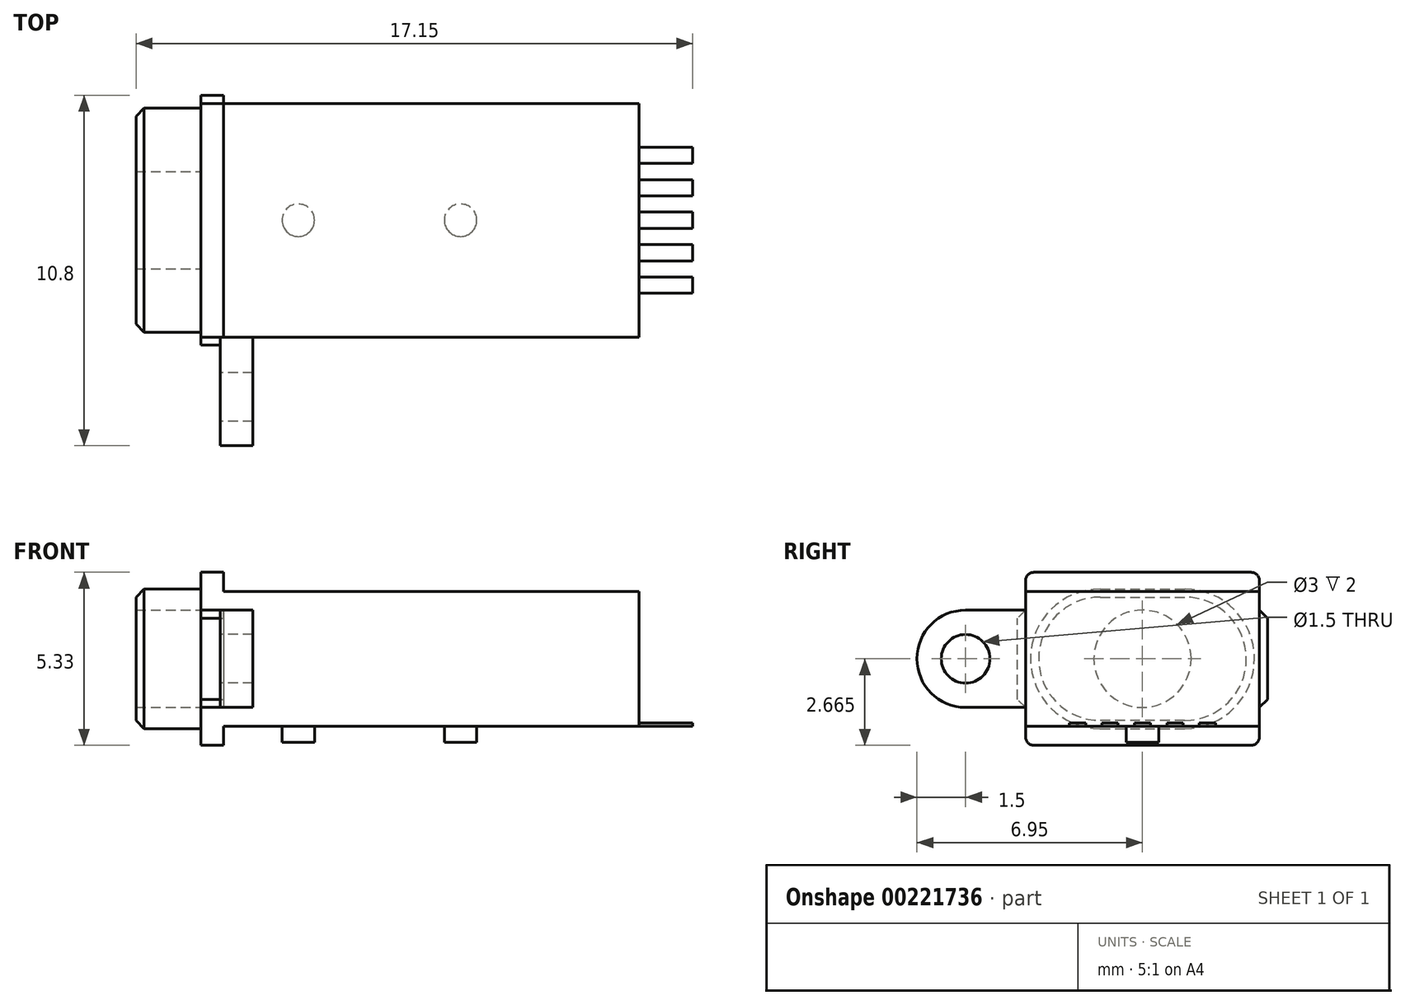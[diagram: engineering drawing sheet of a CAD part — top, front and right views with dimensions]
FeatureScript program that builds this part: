
annotation { "Feature Type Name" : "Feature", "Feature Type Description" : "" }
export const myFeature = defineFeature(function(context is Context, id is Id, definition is map)
    precondition{}
    {
        {
            var Q0;
            Q0=qCreatedBy(makeId("Top.planeOp"),FACE);
            var sketch = newSketch(context, id + "F0", { "sketchPlane" : qUnion([Q0])});
            skLineSegment(sketch, "E0.bottom", {"start": v(0, 3.6) * mm, "end": v(12.8, 3.6) * mm});
            skLineSegment(sketch, "E0.top", {"start": v(0, -3.6) * mm, "end": v(12.8, -3.6) * mm});
            skLineSegment(sketch, "E0.left", {"start": v(0, 3.6) * mm, "end": v(0, -3.6) * mm});
            skLineSegment(sketch, "E0.right", {"start": v(12.8, 3.6) * mm, "end": v(12.8, -3.6) * mm});
            skSolve(sketch);
        }
        {
            var Q0;
            Q0 = qSketchRegion(id + "F0", true);
            extrude(context, id + "F1", {"entities" : qUnion([Q0]), "depth" : 4.15 * mm});
        }
        {
            var Q0;
            Q0=makeQuery(id+"F1.opExtrude","SWEPT_FACE",FACE,{"disambiguationData":[OSD([sQuery(id+"F0.wireOp",EDGE,"E0.left")])]});
            var sketch = newSketch(context, id + "F2", { "sketchPlane" : qUnion([Q0])});
            skLineSegment(sketch, "E1.bottom", {"start": v(-3.35, 4.74) * mm, "end": v(3.35, 4.74) * mm});
            skLineSegment(sketch, "E1.top", {"start": v(-3.35, -0.6) * mm, "end": v(3.35, -0.6) * mm});
            skLineSegment(sketch, "E1.left", {"start": v(-3.6, 4.49) * mm, "end": v(-3.6, -0.34) * mm});
            skLineSegment(sketch, "E1.right", {"start": v(3.6, 4.5) * mm, "end": v(3.6, -0.34) * mm});
            skPoint(sketch, "E1.middle", {"position": v(0, 2.08) * mm});
            skLineSegment(sketch, "E2", {"start": v(0, 0) * mm, "end": v(0, 4.15) * mm, "construction": true});
            skPoint(sketch, "E3.visualSharp", {"position": v(-3.6, 4.74) * mm});
            skArc(sketch, "E3.filletArc", {"start": v(-3.35, 4.74) * mm, "mid": v(-3.53, 4.67) * mm, "end": v(-3.6, 4.49) * mm});
            skPoint(sketch, "E4.visualSharp", {"position": v(3.6, 4.74) * mm});
            skArc(sketch, "E4.filletArc", {"start": v(3.6, 4.5) * mm, "mid": v(3.53, 4.67) * mm, "end": v(3.35, 4.74) * mm});
            skPoint(sketch, "E5.visualSharp", {"position": v(3.6, -0.6) * mm});
            skArc(sketch, "E5.filletArc", {"start": v(3.35, -0.6) * mm, "mid": v(3.53, -0.52) * mm, "end": v(3.6, -0.34) * mm});
            skPoint(sketch, "E6.visualSharp", {"position": v(-3.6, -0.6) * mm});
            skArc(sketch, "E6.filletArc", {"start": v(-3.6, -0.34) * mm, "mid": v(-3.53, -0.52) * mm, "end": v(-3.35, -0.6) * mm});
            skLineSegment(sketch, "E7.bottom", {"start": v(3.85, 3.33) * mm, "end": v(-3.85, 3.32) * mm});
            skLineSegment(sketch, "E7.top", {"start": v(3.85, 0.83) * mm, "end": v(-3.85, 0.82) * mm});
            skLineSegment(sketch, "E7.left", {"start": v(3.85, 3.33) * mm, "end": v(3.85, 0.83) * mm});
            skLineSegment(sketch, "E7.right", {"start": v(-3.85, 3.32) * mm, "end": v(-3.85, 0.82) * mm});
            skLineSegment(sketch, "E8", {"start": v(-3.85, 3.32) * mm, "end": v(-3.6, 3.58) * mm});
            skLineSegment(sketch, "E9", {"start": v(-3.85, 0.82) * mm, "end": v(-3.6, 0.57) * mm});
            skLineSegment(sketch, "E10", {"start": v(3.85, 3.33) * mm, "end": v(3.6, 3.57) * mm});
            skLineSegment(sketch, "E11", {"start": v(3.85, 0.83) * mm, "end": v(3.6, 0.58) * mm});
            skSolve(sketch);
        }
        {
            var Q0;
            Q0 = qSketchRegion(id + "F2", true);
            var Q1;
            {var subQ0=sQuery(id+"F2.wireOp",EDGE,"E7.bottom");var subQ1=sQuery(id+"F2.wireOp",EDGE,"E1.left");var subQ2=makeQuery(id+"F2.imprint","INTERSECT",VERTEX,{"derivedFrom":[subQ1,subQ0]});Q1=makeQuery(id+"F2.imprint","IMPRINT",FACE,{"disambiguationData":[TD([[makeQuery(id+"F2.imprint","IMPRINT",EDGE,{"disambiguationData":[TD([[subQ2,-1.0]])],"derivedFrom":subQ1}),1.0]])]});}
            extrude(context, id + "F3", {"entities" : qUnion([Q0, Q1]), "operationType" : NewBodyOperationType.ADD, "depth" : .7 * mm});
        }
        {
            var Q0;
            Q0=makeQuery(id+"F3.opExtrude","CAP_FACE",FACE,{"disambiguationData":[OSD([sQuery(id+"F2.wireOp",EDGE,"E1.bottom"),sQuery(id+"F2.wireOp",EDGE,"E1.top"),sQuery(id+"F2.wireOp",EDGE,"E1.left"),sQuery(id+"F2.wireOp",EDGE,"E1.right"),sQuery(id+"F2.wireOp",EDGE,"E3.filletArc"),sQuery(id+"F2.wireOp",EDGE,"E4.filletArc"),sQuery(id+"F2.wireOp",EDGE,"E5.filletArc"),sQuery(id+"F2.wireOp",EDGE,"E6.filletArc"),sQuery(id+"F2.wireOp",EDGE,"E7.left"),sQuery(id+"F2.wireOp",EDGE,"E7.right"),sQuery(id+"F2.wireOp",EDGE,"E8"),sQuery(id+"F2.wireOp",EDGE,"E9"),sQuery(id+"F2.wireOp",EDGE,"E10"),sQuery(id+"F2.wireOp",EDGE,"E11")])],"isStart":false});
            var sketch = newSketch(context, id + "F4", { "sketchPlane" : qUnion([Q0])});
            skLineSegment(sketch, "E12.bottom", {"start": v(1.3, 4.22) * mm, "end": v(-1.3, 4.22) * mm});
            skLineSegment(sketch, "E12.top", {"start": v(1.3, -0.08) * mm, "end": v(-1.3, -0.08) * mm});
            skLineSegment(sketch, "E12.left", {"start": v(1.3, 4.23) * mm, "end": v(1.3, -0.08) * mm, "construction": true});
            skLineSegment(sketch, "E12.right", {"start": v(-1.3, 4.23) * mm, "end": v(-1.3, -0.08) * mm, "construction": true});
            skPoint(sketch, "E12.middle", {"position": v(0, 2.07) * mm});
            skArc(sketch, "E13", {"start": v(1.3, -0.08) * mm, "mid": v(3.45, 2.07) * mm, "end": v(1.3, 4.22) * mm});
            skArc(sketch, "E14", {"start": v(-1.3, 4.22) * mm, "mid": v(-3.45, 2.07) * mm, "end": v(-1.3, -0.08) * mm});
            skLineSegment(sketch, "E15", {"start": v(-3.45, 2.07) * mm, "end": v(3.45, 2.08) * mm, "construction": true});
            skCircle(sketch, "E16", {"center": v(0, 2.07) * mm, "radius": 1.5 * mm});
            skSolve(sketch);
        }
        {
            var Q0;
            Q0 = qSketchRegion(id + "F4", true);
            extrude(context, id + "F5", {"entities" : qUnion([Q0]), "operationType" : NewBodyOperationType.ADD, "depth" : 2 * mm});
        }
        {
            var Q0;
            Q0=makeQuery(id+"F5.opExtrude","CAP_EDGE",EDGE,{"disambiguationData":[OSD([sQuery(id+"F4.wireOp",EDGE,"E12.bottom")])],"isStart":false});
            chamfer(context, id + "F6", {"entities" : qUnion([Q0]), "width" : .25 * mm, "tangentPropagation" : true});
        }
        {
            var Q0;
            {var subQ0=sQuery(id+"F2.wireOp",EDGE,"E1.right");var subQ1=sQuery(id+"F0.wireOp",EDGE,"E0.left");var subQ2=makeQuery(id+"F2.imprint","INTERSECT",VERTEX,{"derivedFrom":[makeQuery(id+"F1.opExtrude","CAP_EDGE",EDGE,{"disambiguationData":[OSD([subQ1])],"isStart":true}),subQ0]});var subQ3=makeQuery(id+"F2.imprint","INTERSECT",VERTEX,{"derivedFrom":[makeQuery(id+"F1.opExtrude","CAP_EDGE",EDGE,{"disambiguationData":[OSD([subQ1])],"isStart":false}),subQ0]});Q0=makeQuery(id+"F3.boolean.opBoolean","MERGE",FACE,{"derivedFrom":[makeQuery(id+"F1.opExtrude","SWEPT_FACE",FACE,{"disambiguationData":[OSD([sQuery(id+"F0.wireOp",EDGE,"E0.top")])]}),makeQuery(id+"F3.opExtrude","SWEPT_FACE",FACE,{"disambiguationData":[OSD([subQ0]),TDD([makeQuery(id+"F2.imprint","IMPRINT",EDGE,{"disambiguationData":[TD([[subQ3,1.0]])],"derivedFrom":subQ0}),makeQuery(id+"F2.imprint","IMPRINT",EDGE,{"disambiguationData":[TD([[subQ3,-1.0]])],"derivedFrom":subQ0})])]}),makeQuery(id+"F3.opExtrude","SWEPT_FACE",FACE,{"disambiguationData":[OSD([subQ0]),TDD([makeQuery(id+"F2.imprint","IMPRINT",EDGE,{"disambiguationData":[TD([[subQ2,-1.0]])],"derivedFrom":subQ0}),makeQuery(id+"F2.imprint","IMPRINT",EDGE,{"disambiguationData":[TD([[subQ2,1.0]])],"derivedFrom":subQ0})])]})]});}
            var sketch = newSketch(context, id + "F7", { "sketchPlane" : qUnion([Q0])});
            skLineSegment(sketch, "E17.bottom", {"start": v(-0.1, 3.58) * mm, "end": v(0.9, 3.58) * mm});
            skLineSegment(sketch, "E17.top", {"start": v(-0.1, 0.58) * mm, "end": v(0.9, 0.58) * mm});
            skLineSegment(sketch, "E17.left", {"start": v(-0.1, 3.58) * mm, "end": v(-0.1, 0.58) * mm});
            skLineSegment(sketch, "E17.right", {"start": v(0.9, 3.58) * mm, "end": v(0.9, 0.58) * mm});
            skLineSegment(sketch, "E18", {"start": v(-0.1, 2.08) * mm, "end": v(12.8, 2.08) * mm, "construction": true});
            skSolve(sketch);
        }
        {
            var Q0;
            Q0 = qSketchRegion(id + "F7", true);
            extrude(context, id + "F8", {"entities" : qUnion([Q0]), "operationType" : NewBodyOperationType.ADD, "depth" : 3.35 * mm});
        }
        {
            var Q0;
            Q0=makeQuery(id+"F8.opExtrude","CAP_EDGE",EDGE,{"disambiguationData":[OSD([sQuery(id+"F7.wireOp",EDGE,"E17.bottom")])],"isStart":false});
            var Q1;
            Q1=makeQuery(id+"F8.opExtrude","CAP_EDGE",EDGE,{"disambiguationData":[OSD([sQuery(id+"F7.wireOp",EDGE,"E17.top")])],"isStart":false});
            fillet(context, id + "F9", {"entities" : qUnion([Q0, Q1]), "radius" : 1.5 * mm, "tangentPropagation" : true, "allowEdgeOverflow" : false});
        }
        {
            var Q0;
            Q0=makeQuery(id+"F8.opExtrude","SWEPT_FACE",FACE,{"disambiguationData":[OSD([sQuery(id+"F7.wireOp",EDGE,"E17.left")])]});
            var sketch = newSketch(context, id + "F10", { "sketchPlane" : qUnion([Q0])});
            skCircle(sketch, "E19", {"center": v(5.45, 2.08) * mm, "radius": 0.75 * mm});
            skSolve(sketch);
        }
        {
            var Q0;
            Q0 = qSketchRegion(id + "F10", true);
            extrude(context, id + "F11", {"entities" : qUnion([Q0]), "operationType" : NewBodyOperationType.REMOVE, "oppositeDirection" : true, "depth" : 25 * mm});
        }
        {
            var Q0;
            Q0=makeQuery(id+"F1.opExtrude","CAP_FACE",FACE,{"disambiguationData":[OSD([sQuery(id+"F0.wireOp",EDGE,"E0.bottom"),sQuery(id+"F0.wireOp",EDGE,"E0.top"),sQuery(id+"F0.wireOp",EDGE,"E0.left"),sQuery(id+"F0.wireOp",EDGE,"E0.right")])],"isStart":true});
            var sketch = newSketch(context, id + "F12", { "sketchPlane" : qUnion([Q0])});
            skCircle(sketch, "E20", {"center": v(2.3, 0) * mm, "radius": 0.5 * mm});
            skCircle(sketch, "E21", {"center": v(7.3, 0) * mm, "radius": 0.5 * mm});
            skSolve(sketch);
        }
        {
            var Q0;
            Q0 = qSketchRegion(id + "F12", true);
            extrude(context, id + "F13", {"entities" : qUnion([Q0]), "operationType" : NewBodyOperationType.ADD, "depth" : .5 * mm});
        }
        {
            var Q0;
            {var subQ1=sQuery(id+"F2.wireOp",EDGE,"E4.filletArc");var subQ4=sQuery(id+"F2.wireOp",EDGE,"E1.bottom");var subQ5=sQuery(id+"F2.wireOp",EDGE,"E1.right");var subQ8=sQuery(id+"F2.wireOp",EDGE,"E10");var subQ9=sQuery(id+"F2.wireOp",EDGE,"E1.left");var subQ11=sQuery(id+"F2.wireOp",EDGE,"E8");var subQ12=sQuery(id+"F2.wireOp",EDGE,"E3.filletArc");var subQ15=sQuery(id+"F2.wireOp",EDGE,"E9");var subQ16=sQuery(id+"F2.wireOp",EDGE,"E6.filletArc");var subQ18=sQuery(id+"F2.wireOp",EDGE,"E11");var subQ19=sQuery(id+"F2.wireOp",EDGE,"E5.filletArc");Q0=makeQuery(id+"F3.boolean.opBoolean","SPLIT",FACE,{"disambiguationData":[TD([makeQuery(id+"F3.opExtrude","SWEPT_FACE",FACE,{"disambiguationData":[OSD([subQ4])]})])],"derivedFrom":makeQuery(id+"F3.opExtrude","CAP_FACE",FACE,{"disambiguationData":[OSD([subQ4,sQuery(id+"F2.wireOp",EDGE,"E1.top"),subQ9,subQ5,subQ12,subQ1,subQ19,subQ16,sQuery(id+"F2.wireOp",EDGE,"E7.left"),sQuery(id+"F2.wireOp",EDGE,"E7.right"),subQ11,subQ15,subQ8,subQ18])],"isStart":true})});}
            var sketch = newSketch(context, id + "F14", { "sketchPlane" : qUnion([Q0])});
            skLineSegment(sketch, "E22.bottom", {"start": v(-0.25, 0) * mm, "end": v(0.25, 0) * mm});
            skLineSegment(sketch, "E22.top", {"start": v(-0.25, 0.1) * mm, "end": v(0.25, 0.1) * mm});
            skLineSegment(sketch, "E22.left", {"start": v(-0.25, 0) * mm, "end": v(-0.25, 0.1) * mm});
            skLineSegment(sketch, "E22.right", {"start": v(0.25, 0) * mm, "end": v(0.25, 0.1) * mm});
            skLineSegment(sketch, "E23.bottom", {"start": v(0.75, 0.1) * mm, "end": v(1.25, 0.1) * mm});
            skLineSegment(sketch, "E23.top", {"start": v(0.75, 0) * mm, "end": v(1.25, 0) * mm});
            skLineSegment(sketch, "E23.left", {"start": v(0.75, 0.1) * mm, "end": v(0.75, 0) * mm});
            skLineSegment(sketch, "E23.right", {"start": v(1.25, 0.1) * mm, "end": v(1.25, 0) * mm});
            skLineSegment(sketch, "E24.bottom", {"start": v(1.75, 0.1) * mm, "end": v(2.25, 0.1) * mm});
            skLineSegment(sketch, "E24.top", {"start": v(1.75, 0) * mm, "end": v(2.25, 0) * mm});
            skLineSegment(sketch, "E24.left", {"start": v(1.75, 0.1) * mm, "end": v(1.75, 0) * mm});
            skLineSegment(sketch, "E24.right", {"start": v(2.25, 0.1) * mm, "end": v(2.25, 0) * mm});
            skLineSegment(sketch, "E25.bottom", {"start": v(-0.75, 0.1) * mm, "end": v(-1.25, 0.1) * mm});
            skLineSegment(sketch, "E25.top", {"start": v(-0.75, 0) * mm, "end": v(-1.25, 0) * mm});
            skLineSegment(sketch, "E25.left", {"start": v(-0.75, 0.1) * mm, "end": v(-0.75, 0) * mm});
            skLineSegment(sketch, "E25.right", {"start": v(-1.25, 0.1) * mm, "end": v(-1.25, 0) * mm});
            skLineSegment(sketch, "E26.bottom", {"start": v(-1.75, 0.1) * mm, "end": v(-2.25, 0.1) * mm});
            skLineSegment(sketch, "E26.top", {"start": v(-1.75, 0) * mm, "end": v(-2.25, 0) * mm});
            skLineSegment(sketch, "E26.left", {"start": v(-1.75, 0.1) * mm, "end": v(-1.75, 0) * mm});
            skLineSegment(sketch, "E26.right", {"start": v(-2.25, 0.1) * mm, "end": v(-2.25, 0) * mm});
            skLineSegment(sketch, "E27", {"start": v(-1, 0.1) * mm, "end": v(-1, 0) * mm, "construction": true});
            skLineSegment(sketch, "E28", {"start": v(-2, 0.1) * mm, "end": v(-2, 0) * mm, "construction": true});
            skLineSegment(sketch, "E29", {"start": v(1, 0.1) * mm, "end": v(1, 0) * mm, "construction": true});
            skLineSegment(sketch, "E30", {"start": v(2, 0.1) * mm, "end": v(2, 0) * mm, "construction": true});
            skLineSegment(sketch, "E31", {"start": v(-1, 0.1) * mm, "end": v(0, 4.15) * mm, "construction": true});
            skLineSegment(sketch, "E32", {"start": v(0, 4.15) * mm, "end": v(1, 0.1) * mm, "construction": true});
            skLineSegment(sketch, "E33", {"start": v(-2, 0.1) * mm, "end": v(0, 4.15) * mm, "construction": true});
            skLineSegment(sketch, "E34", {"start": v(2, 0.1) * mm, "end": v(0, 4.15) * mm, "construction": true});
            skSolve(sketch);
        }
        {
            var Q0;
            Q0 = qSketchRegion(id + "F14", true);
            extrude(context, id + "F15", {"entities" : qUnion([Q0]), "operationType" : NewBodyOperationType.ADD, "depth" : 14.45 * mm});
        }
    });
